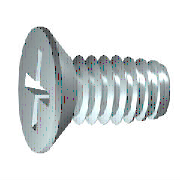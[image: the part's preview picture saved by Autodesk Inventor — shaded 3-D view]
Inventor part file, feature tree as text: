
AUTODESK INVENTOR PART (.ipt)
format: ipt  version: 2020 (Build 240168000, 168)  size: 233,984 bytes
history: native  units: mm (DEFAULTED — no unit token found)
features: sketch x2, extrude x1, plane x1
ambient origin geometry x8: Origin, YZ Plane, XZ Plane, XY Plane, X Axis, Y Axis, Z Axis, Center Point
bodies: Solid1 (feature_tree), Body (feature_tree)
feature tree (4):
  sketch  "Sketch1"  dims[d0=45.0mm d1=5.25mm d2=9.5mm d3=18.3mm]
  sketch  "Sketch2"  dims[d8=90.0deg d4=5.7mm d5=10.0mm d6=4.625123mm d7=10.821041mm d9=39.75mm d10=0.0mm d11=1.03mm d12=4.2mm d13=45.0deg d14=5.25mm d15=45.0mm d45=5.7mm d16=0.174533mm d17=10.0mm d18=45.0deg d19=3.0mm d20=3.5mm d21=10.0mm d22=0.595mm d24=0.0mm d25=0.238mm d62=45.0deg d64=0.0mm d65=0.0mm]
  extrude  "Slot"  Depth=18.3mm
  plane  "Work Plane2"
